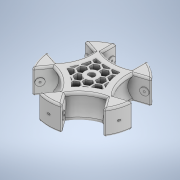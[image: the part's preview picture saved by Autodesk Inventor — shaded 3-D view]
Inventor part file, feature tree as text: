
AUTODESK INVENTOR PART (.ipt)
format: ipt  version: 2021 (Build 250183000, 183)  size: 1,001,472 bytes
history: native  units: in
note: dims shown in document units (in); Inventor stores cm internally (conversion verified against a paired STEP export)
features: revolve x5, extrude x3, fillet x3, mirror x1, sketch x1
ambient origin geometry x8: Origin, YZ Plane, XZ Plane, XY Plane, X Axis, Y Axis, Z Axis, Center Point
bodies: Solid2 (feature_tree)
feature tree (13):
  extrude  "Extrusion6"  Depth=0.3937in
  revolve  "Revolution12"  [1 undecoded]
  revolve  "Revolution13"  [1 undecoded]
  revolve  "Revolution14"  [1 undecoded]
  revolve  "Revolution15"  [1 undecoded]
  revolve  "Revolution16"  [1 undecoded]
  mirror  "Mirror1"
  extrude  "Extrusion9"  Depth=0.2598in TaperAngle=0.0deg
  fillet  "Fillet8"  Radius=0.1181in
  fillet  "Fillet9"  Radius=0.096in
  fillet  "Fillet10"  [1 undecoded]
  extrude  "Extrusion10"  Depth=0.3937in
  sketch  "Sketch4"  dims[d0=1.9685in d51=0.0787in d52=0.5906in d54=0.0787in d56=0.6299in d58=0.0787in d59=0.0354in d60=0.2598in d61=0.0in d83=0.1181in d84=0.096in d85=0.0in d86=0.0in d87=0.6004in d96=90.0deg d97=1.9685in d99=360.0deg d101=90.0deg d102=90.0deg d103=90.0deg d104=90.0deg d105=0.0394in d106=0.0079in d107=0.0197in d108=0.0787in d109=0.0787in d110=0.0787in d111=0.0787in d112=0.0787in d113=0.0787in d114=0.1575in d122=1.1811in d124=0.1969in d125=0.3937in d127=1.0in d129=1.1811in d131=0.1969in d132=0.3937in d134=1.0in d136=1.1811in d138=0.1969in d139=0.3937in d141=1.0in d143=1.1811in d145=0.1969in d146=0.3937in d148=1.0in d150=0.0in d151=0.0in d35=0.5in d36=0.0344in d37=0.5in d38=0.0344in d77=0.0344in d78=0.0344in]
note: 6 required parameter values undecoded (feature->parameter linkage not recoverable at this tier; creation-order binding heuristic only, values carry confidence <= 0.55)